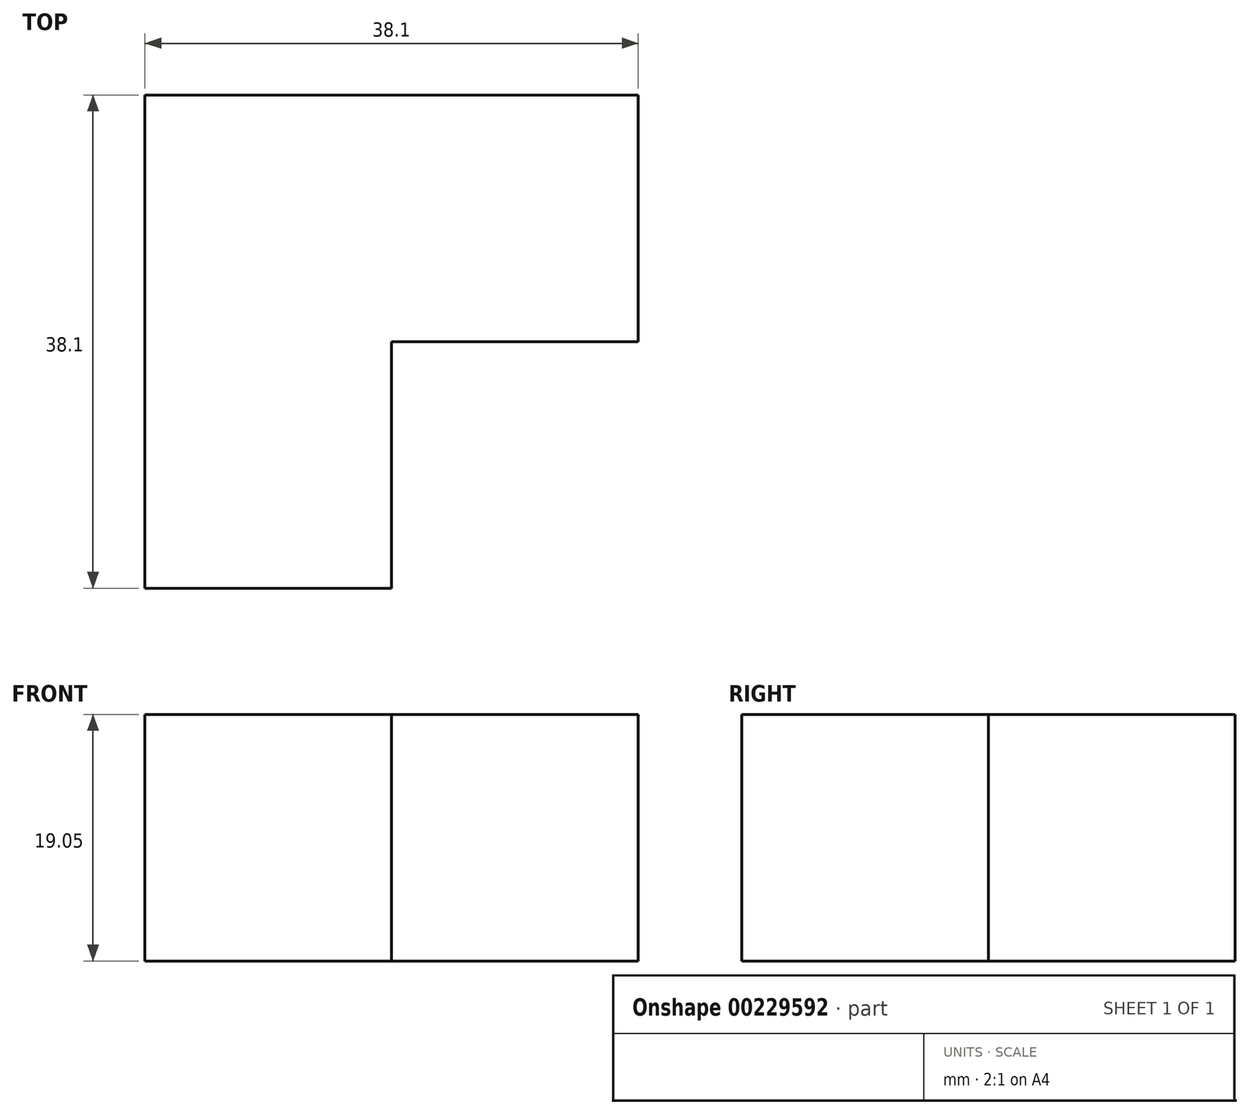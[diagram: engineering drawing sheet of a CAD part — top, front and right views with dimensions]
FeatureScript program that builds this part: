
annotation { "Feature Type Name" : "Feature", "Feature Type Description" : "" }
export const myFeature = defineFeature(function(context is Context, id is Id, definition is map)
    precondition{}
    {
        {
            var Q0;
            Q0=qCreatedBy(makeId("Top.planeOp"),FACE);
            var sketch = newSketch(context, id + "F0", { "sketchPlane" : qUnion([Q0])});
            skLineSegment(sketch, "E0", {"start": v(0, 0) * mm, "end": v(0, 38.1) * mm});
            skLineSegment(sketch, "E1", {"start": v(0, 38.1) * mm, "end": v(38.1, 38.1) * mm});
            skLineSegment(sketch, "E2", {"start": v(38.1, 38.1) * mm, "end": v(38.1, 19.05) * mm});
            skLineSegment(sketch, "E3", {"start": v(38.1, 19.05) * mm, "end": v(19.05, 19.05) * mm});
            skLineSegment(sketch, "E4", {"start": v(0, 0) * mm, "end": v(19.05, 0) * mm});
            skLineSegment(sketch, "E5", {"start": v(19.05, 19.05) * mm, "end": v(19.05, 0) * mm});
            skSolve(sketch);
        }
        {
            var Q0;
            Q0 = qSketchRegion(id + "F0", true);
            extrude(context, id + "F1", {"entities" : qUnion([Q0]), "depth" : 19.05 * mm});
        }
    });
